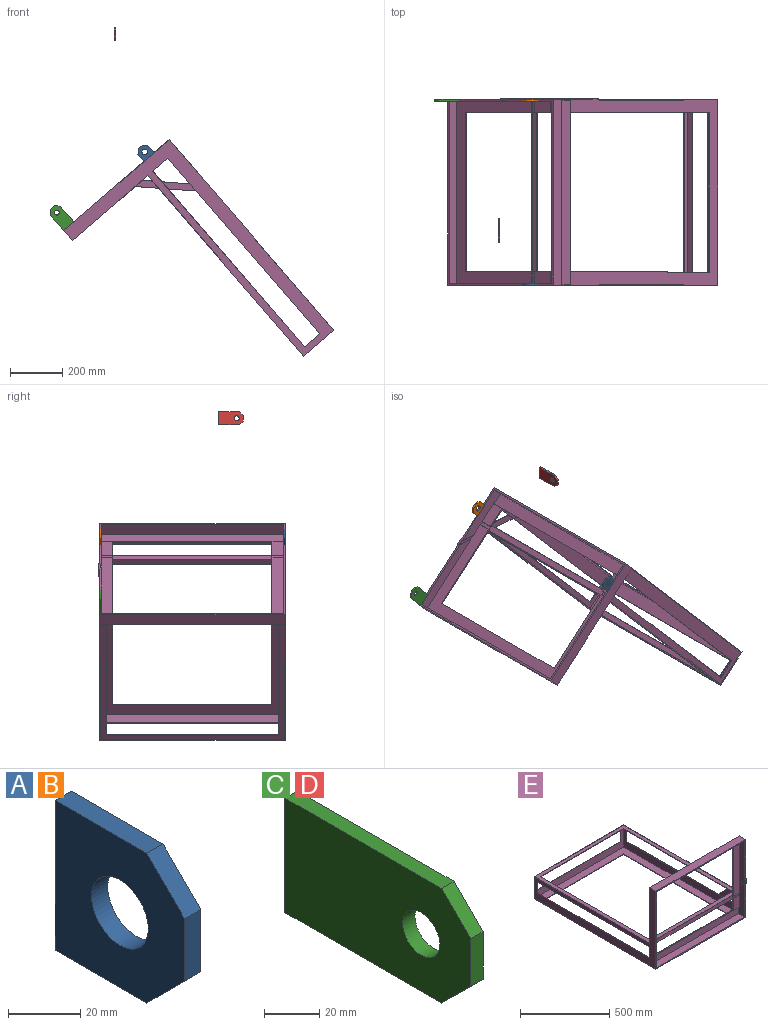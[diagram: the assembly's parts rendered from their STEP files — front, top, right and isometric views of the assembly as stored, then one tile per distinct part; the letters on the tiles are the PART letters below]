
ASSEMBLY  parts=5 mates=3
PART A: 9 faces, bbox 6.4x50.8x50.8 mm
  f0: plane 35.92x6.35mm, normal (0,0,1), area 228.1mm2, adj f1,f5,f7,f8
  f1: plane 14.88x14.88mm, normal (0,-0.71,0.71), area 133.6mm2, adj f0,f2,f7,f8
  f2: plane 21.04x6.35mm, normal (0,-1,0), area 133.6mm2, adj f1,f3,f7,f8
  f3: plane 14.88x14.88mm, normal (0,-0.71,-0.71), area 133.6mm2, adj f2,f4,f7,f8
  f4: plane 35.92x6.35mm, normal (0,0,-1), area 228.1mm2, adj f3,f5,f7,f8
  f5: plane 50.8x6.35mm, normal (0,1,0), area 322.6mm2, adj f0,f4,f7,f8
  f6: cylinder r=11.11mm len=22.23mm, axis (-1,0,0), area 443.4mm2, adj f7,f8
  f7: plane 50.8x50.8mm, normal (1,0,0), area 1971.3mm2, adj f0,f1,f2,f3,f4,f5,f6
  f8: plane 50.8x50.8mm, normal (-1,0,0), area 1971.3mm2, adj f0,f1,f2,f3,f4,f5,f6
PART B: same geometry as A
PART C: 9 faces, bbox 6.4x95.3x50.8 mm
  f0: plane 80.37x6.35mm, normal (0,0,1), area 510.4mm2, adj f1,f5,f7,f8
  f1: plane 14.88x14.88mm, normal (0,-0.71,0.71), area 133.6mm2, adj f0,f2,f7,f8
  f2: plane 21.04x6.35mm, normal (0,-1,0), area 133.6mm2, adj f1,f3,f7,f8
  f3: plane 14.88x14.88mm, normal (0,-0.71,-0.71), area 133.6mm2, adj f2,f4,f7,f8
  f4: plane 80.37x6.35mm, normal (0,0,-1), area 510.4mm2, adj f3,f5,f7,f8
  f5: plane 50.8x6.35mm, normal (0,1,0), area 322.6mm2, adj f0,f4,f7,f8
  f6: cylinder r=9.53mm len=19.05mm, axis (-1,0,0), area 380mm2, adj f7,f8
  f7: plane 95.25x50.8mm, normal (1,0,0), area 4332.3mm2, adj f0,f1,f2,f3,f4,f5,f6
  f8: plane 95.25x50.8mm, normal (-1,0,0), area 4332.3mm2, adj f0,f1,f2,f3,f4,f5,f6
PART D: same geometry as C
PART E: 69 faces, bbox 714.4x965.2x533.5 mm
  f0: plane 714.38x533.4mm, normal (0,-1,0), area 15702.2mm2, adj f5,f7,f10,f20,f21,f45,f46,f47
  f1: plane 892.18x711.2mm, normal (0,0,1), area 9818.5mm2, adj f2,f4,f6,f7,f8,f9,f21,f22
  f2: plane 431.8x6.35mm, normal (-1,0,0), area 2701.6mm2, adj f1,f3,f9,f14,f34,f52,f55,f59
  f3: plane 609.6x6.35mm, normal (0,0,-1), area 3871mm2, adj f2,f4,f14,f61
  f4: plane 431.8x6.35mm, normal (1,0,0), area 2701.6mm2, adj f1,f3,f8,f14,f34,f49,f50,f51
  f5: plane 317.5x50.8mm, normal (1,0,0), area 14838.7mm2, adj f0,f14,f20,f45
  f6: plane 850.9x152.4mm, normal (1,0,0), area 59999.9mm2, adj f1,f10,f19,f23,f28,f32,f45
  f7: plane 230.78x230.78mm, normal (1,0,0), area 19308.9mm2, adj f0,f1,f9,f10,f14,f19,f28,f46
  f8: plane 76.2x50.8mm, normal (0,1,0), area 3871mm2, adj f1,f4,f19,f21
  f9: plane 76.2x50.8mm, normal (0,1,0), area 3871mm2, adj f1,f2,f7,f19
  f10: plane 965.2x714.38mm, normal (0,0,-1), area 155275mm2, adj f0,f6,f7,f11,f12,f21,f23,f24
  f11: plane 860.43x3.18mm, normal (1,0,0), area 2587mm2, adj f10,f13,f24,f37,f41,f42
  f12: plane 860.43x3.18mm, normal (-1,0,0), area 2587mm2, adj f10,f13,f24,f37,f41,f42
  f13: plane 908.05x704.85mm, normal (0,0,1), area 115524mm2, adj f11,f12,f22,f24,f25,f26,f41
  f14: plane 711.2x381mm, normal (0,1,0), area 69677.3mm2, adj f2,f3,f4,f5,f7,f20,f21,f28
  f15: plane 863.6x3.18mm, normal (1,0,0), area 2741.9mm2, adj f27,f28,f29,f35
  f16: plane 863.6x3.18mm, normal (-1,0,0), area 2741.9mm2, adj f27,f28,f29,f35
  f17: plane 660.4x3.18mm, normal (0,0,1), area 2096.8mm2, adj f23,f25,f30,f33
  f18: plane 660.4x3.18mm, normal (0,0,-1), area 2096.8mm2, adj f23,f25,f30,f33
  f19: plane 889x711.2mm, normal (0,0,-1), area 7883mm2, adj f6,f7,f8,f9,f21,f22,f26,f31
  f20: plane 711.2x50.8mm, normal (0,0,1), area 36129mm2, adj f0,f5,f14,f21
  f21: plane 965.2x533.4mm, normal (-1,0,0), area 98709.5mm2, adj f0,f1,f8,f10,f14,f19,f20,f23
  f22: plane 908.05x146.05mm, normal (1,0,0), area 65120.8mm2, adj f1,f13,f19,f25,f29,f31,f36,f41
  f23: plane 711.2x152.4mm, normal (0,1,0), area 58064.4mm2, adj f6,f10,f17,f18,f21,f28,f30,f33
  f24: plane 609.6x3.18mm, normal (0,-1,0), area 1935.5mm2, adj f10,f11,f12,f13
  f25: plane 704.85x146.05mm, normal (0,-1,0), area 52620.9mm2, adj f13,f17,f18,f22,f26,f29,f30,f33
  f26: plane 908.05x146.05mm, normal (-1,0,0), area 65120.8mm2, adj f1,f13,f19,f25,f29,f32,f36,f41
  f27: plane 660.4x3.18mm, normal (0,-1,0), area 2096.8mm2, adj f15,f16,f28,f29
  f28: plane 914.4x711.2mm, normal (0,0,1), area 79999.8mm2, adj f6,f7,f14,f15,f16,f21,f23,f27
  f29: plane 908.05x704.85mm, normal (0,0,-1), area 69717.6mm2, adj f15,f16,f22,f25,f26,f27,f35,f36
  f30: plane 76.2x3.18mm, normal (1,0,0), area 241.9mm2, adj f17,f18,f23,f25
  f31: plane 76.2x3.18mm, normal (0,-1,0), area 241.9mm2, adj f1,f19,f21,f22
  f32: plane 76.2x3.18mm, normal (0,-1,0), area 241.9mm2, adj f1,f6,f19,f26
  f33: plane 76.2x3.18mm, normal (-1,0,0), area 241.9mm2, adj f17,f18,f23,f25
  f34: plane 609.6x25.4mm, normal (0,-1,0), area 15483.8mm2, adj f2,f4,f19,f28
  f35: plane 660.4x3.18mm, normal (0,1,0), area 2096.8mm2, adj f15,f16,f28,f29
  f36: plane 704.85x22.23mm, normal (0,1,0), area 15665.3mm2, adj f19,f22,f26,f29
  f37: plane 704.85x3.18mm, normal (0,1,0), area 1948.1mm2, adj f10,f11,f12,f38,f39,f42,f43
  f38: plane 50.8x0.13mm, normal (-1,0,0), area 6.7mm2, adj f10,f37,f40,f43
  f39: plane 50.8x0.13mm, normal (1,0,0), area 6.7mm2, adj f10,f37,f40,f43
  f40: plane 704.85x0.13mm, normal (0,-1,0), area 93.4mm2, adj f10,f38,f39,f43
  f41: plane 704.85x47.76mm, normal (0,1,0), area 33649.3mm2, adj f1,f11,f12,f13,f22,f26,f42
  f42: plane 609.6x47.63mm, normal (0,0,1), area 29032.2mm2, adj f11,f12,f37,f41
  f43: plane 704.85x50.8mm, normal (0,0,-1), area 35806.4mm2, adj f37,f38,f39,f40
  f44: plane 112.12x76.2mm, normal (-1,0,0), area 2737.2mm2, adj f1,f19,f45,f46
  f45: plane 266.7x266.7mm, normal (0,0.71,0.71), area 1197.5mm2, adj f0,f5,f6,f10,f44,f47,f48
  f46: plane 230.78x230.78mm, normal (0,-0.71,-0.71), area 1036.2mm2, adj f0,f7,f10,f44,f47,f48
  f47: plane 266.7x266.7mm, normal (1,0,0), area 8935mm2, adj f0,f10,f45,f46
  f48: plane 63.5x63.5mm, normal (-1,0,0), area 1635.8mm2, adj f14,f28,f45,f46
  f49: plane 44.45x3.18mm, normal (0,0,-1), area 141.1mm2, adj f4,f58,f63,f66
  f50: plane 44.45x12.7mm, normal (0,-1,0), area 564.5mm2, adj f4,f51,f54,f63
  f51: plane 44.45x3.18mm, normal (0,0,-1), area 141.1mm2, adj f4,f50,f61,f63
  f52: plane 44.45x3.18mm, normal (0,0,-1), area 141.1mm2, adj f2,f57,f59,f66
  f53: plane 44.45x44.45mm, normal (0,0.71,0.71), area 199.6mm2, adj f0,f57,f61,f68
  f54: plane 44.45x3.18mm, normal (0,0,1), area 141.1mm2, adj f4,f50,f58,f63
  f55: plane 44.45x3.18mm, normal (0,0,1), area 141.1mm2, adj f2,f57,f59,f65
  f56: plane 313.78x44.45mm, normal (-1,0,0), area 12959.6mm2, adj f0,f61,f62,f67
  f57: plane 233.41x47.63mm, normal (-1,0,0), area 9568.6mm2, adj f0,f52,f53,f55,f59,f60,f61,f64
  f58: plane 82.55x44.45mm, normal (0,-1,0), area 3669.3mm2, adj f4,f49,f54,f63
  f59: plane 82.55x44.45mm, normal (0,-1,0), area 3669.3mm2, adj f2,f52,f55,f57
  f60: plane 698.5x47.63mm, normal (0,0,1), area 33266.1mm2, adj f0,f57,f63,f66
  f61: plane 701.68x381mm, normal (0,-1,0), area 61024.6mm2, adj f2,f3,f4,f51,f53,f56,f57,f62
  f62: plane 698.5x44.45mm, normal (0,0,-1), area 31048.3mm2, adj f0,f56,f61,f63
  f63: plane 520.7x47.63mm, normal (1,0,0), area 23326.6mm2, adj f0,f49,f50,f51,f54,f58,f60,f61
  f64: plane 44.45x3.18mm, normal (0,0,-1), area 141.1mm2, adj f2,f57,f61,f65
  f65: plane 44.45x12.7mm, normal (0,-1,0), area 564.5mm2, adj f2,f55,f57,f64
  f66: plane 698.5x44.45mm, normal (0,-1,0), area 31048.3mm2, adj f1,f49,f52,f57,f60,f63
  f67: plane 44.45x44.45mm, normal (0,-0.71,-0.71), area 199.6mm2, adj f0,f56,f61,f68
  f68: plane 62.41x44.45mm, normal (-1,0,0), area 798.3mm2, adj f0,f53,f61,f67
PLACE A rot(axis=(-0.38,0.38,-0.84),100deg) t=(37.3,-340.97,373.02)mm
PLACE B rot(axis=(-0.38,0.38,-0.84),100deg) t=(37.3,363.88,373.02)mm
PLACE C rot(axis=(-0.38,0.38,-0.84),100deg) t=(-299.29,363.88,140.98)mm
PLACE D t=(-86.69,-145.95,834.08)mm
PLACE E rot(axis=(-0.67,-0.67,0.31),145.8deg) t=(126.02,-298.71,369.44)mm
MATE fastened C.f5 <-> E.f0  axis (0.65,0,-0.76) through (-279.91,363.88,85.88)mm
MATE fastened A.f5 <-> E.f0  axis (0.65,0,-0.76) through (66.06,-347.32,384.77)mm
MATE fastened B.f5 <-> E.f0  axis (0.65,0,-0.76) through (66.06,363.88,384.77)mm
